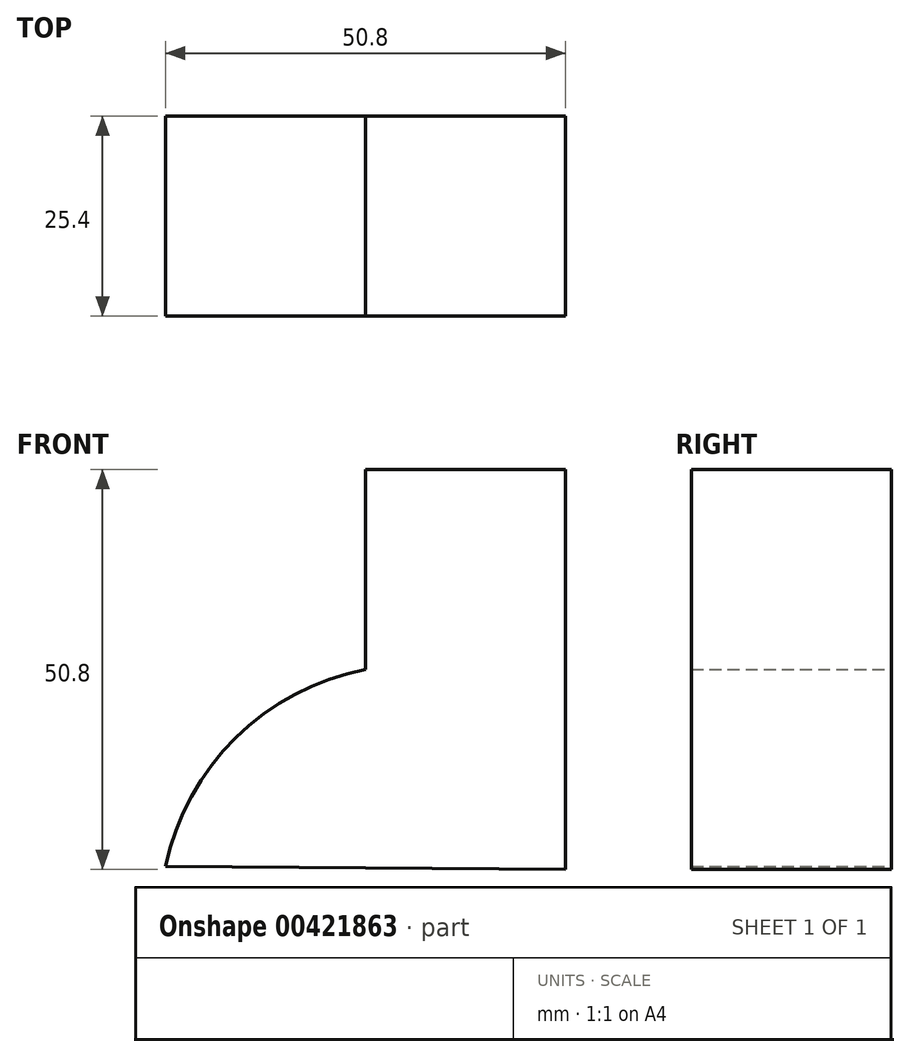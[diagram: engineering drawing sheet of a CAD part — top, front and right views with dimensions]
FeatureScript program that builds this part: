
annotation { "Feature Type Name" : "Feature", "Feature Type Description" : "" }
export const myFeature = defineFeature(function(context is Context, id is Id, definition is map)
    precondition{}
    {
        {
            var Q0;
            Q0=qCreatedBy(makeId("Front.planeOp"),FACE);
            var sketch = newSketch(context, id + "F0", { "sketchPlane" : qUnion([Q0])});
            skLineSegment(sketch, "E0", {"start": v(25.4, 50.44) * mm, "end": v(50.8, 50.44) * mm});
            skLineSegment(sketch, "E1", {"start": v(50.8, 50.44) * mm, "end": v(50.8, -0.36) * mm});
            skLineSegment(sketch, "E2", {"start": v(50.8, -0.36) * mm, "end": v(0, 0) * mm});
            skLineSegment(sketch, "E3", {"start": v(25.4, 50.44) * mm, "end": v(25.4, 25.04) * mm});
            skArc(sketch, "E4", {"start": v(25.4, 25.04) * mm, "mid": v(8.91, 16.36) * mm, "end": v(0, 0) * mm});
            skSolve(sketch);
        }
        {
            var Q0;
            Q0=makeQuery(id+"F0.imprint","IMPRINT",FACE,{"disambiguationData":[TD([[makeQuery(id+"F0.imprint","IMPRINT",EDGE,{"derivedFrom":sQuery(id+"F0.wireOp",EDGE,"E0")}),-1.0]])]});
            extrude(context, id + "F1", {"entities" : qUnion([Q0]), "depth" : 25.4 * mm});
        }
    });
